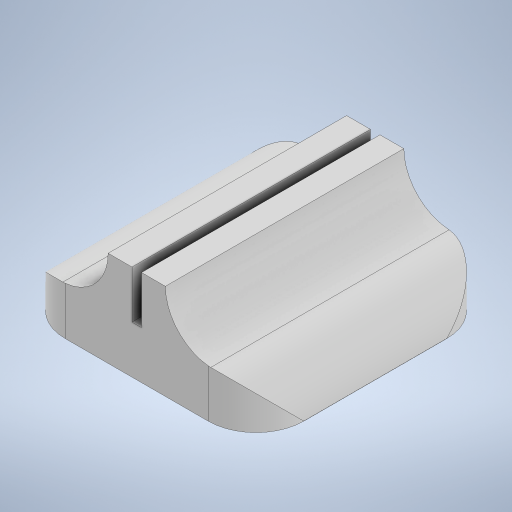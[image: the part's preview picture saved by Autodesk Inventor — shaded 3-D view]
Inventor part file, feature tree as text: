
AUTODESK INVENTOR PART (.ipt)
format: ipt  version: 2024.2 (Build 282272000, 272)  size: 275,456 bytes
history: native  units: mm
features: extrude x2, fillet x2, sketch x2
ambient origin geometry x8: Origin, YZ Plane, XZ Plane, XY Plane, X Axis, Y Axis, Z Axis, Center Point
bodies: Solid1 (feature_tree)
feature tree (6):
  extrude  "Extrusion1"  Depth=50.0mm
  extrude  "Extrusion2"  Depth=10.0mm
  fillet  "Fillet1"  Radius=5.0mm
  fillet  "Fillet2"  Radius=2.0mm
  sketch  "Sketch1"  dims[d0=50.0mm d1=50.0mm]
  sketch  "Sketch2"  dims[d2=10.0mm d3=0.0mm d7=5.0mm d8=5.0mm d9=2.0mm d10=19.0mm d11=10.0mm d12=0.0mm d13=10.0mm d14=10.0mm]
